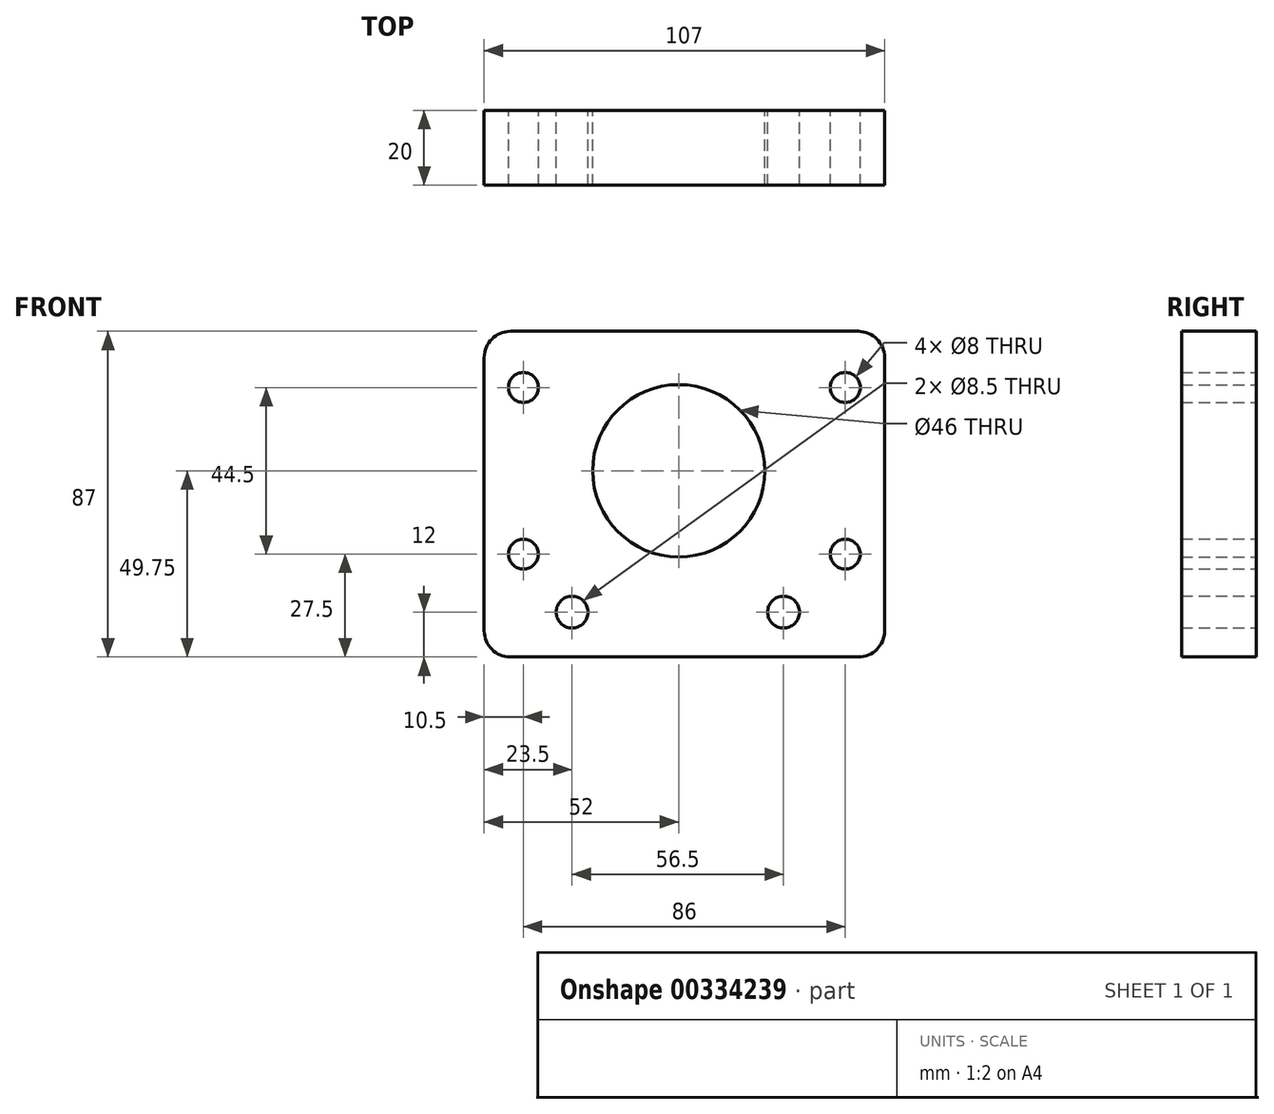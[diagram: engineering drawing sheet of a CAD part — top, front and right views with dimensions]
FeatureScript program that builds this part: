
annotation { "Feature Type Name" : "Feature", "Feature Type Description" : "" }
export const myFeature = defineFeature(function(context is Context, id is Id, definition is map)
    precondition{}
    {
        {
            var Q0;
            Q0=qCreatedBy(makeId("Front.planeOp"),FACE);
            var sketch = newSketch(context, id + "F0", { "sketchPlane" : qUnion([Q0])});
            skCircle(sketch, "E0", {"center": v(0, 0) * mm, "radius": 3.35 * mm});
            skCircle(sketch, "E1", {"center": v(56.5, 0) * mm, "radius": 3.35 * mm});
            skCircle(sketch, "E2", {"center": v(0, -65) * mm, "radius": 4.25 * mm});
            skCircle(sketch, "E3", {"center": v(56.5, -65) * mm, "radius": 4.25 * mm});
            skCircle(sketch, "E4", {"center": v(28.5, -27.25) * mm, "radius": 23 * mm});
            skCircle(sketch, "E5", {"center": v(-13, -49.5) * mm, "radius": 4 * mm});
            skCircle(sketch, "E6", {"center": v(-13, -5) * mm, "radius": 4 * mm});
            skCircle(sketch, "E7", {"center": v(73, -5) * mm, "radius": 4 * mm});
            skCircle(sketch, "E8", {"center": v(73, -49.5) * mm, "radius": 4 * mm});
            skLineSegment(sketch, "E9.bottom", {"start": v(-16.5, 10) * mm, "end": v(76.5, 10) * mm});
            skLineSegment(sketch, "E9.top", {"start": v(-16.5, -77) * mm, "end": v(76.5, -77) * mm});
            skLineSegment(sketch, "E9.left", {"start": v(-23.5, 3) * mm, "end": v(-23.5, -70) * mm});
            skLineSegment(sketch, "E9.right", {"start": v(83.5, 3) * mm, "end": v(83.5, -70) * mm});
            skPoint(sketch, "E10.visualSharp", {"position": v(-23.5, 10) * mm});
            skArc(sketch, "E10.filletArc", {"start": v(-16.5, 10) * mm, "mid": v(-21.45, 7.95) * mm, "end": v(-23.5, 3) * mm});
            skPoint(sketch, "E11.visualSharp", {"position": v(83.5, 10) * mm});
            skArc(sketch, "E11.filletArc", {"start": v(83.5, 3) * mm, "mid": v(81.45, 7.95) * mm, "end": v(76.5, 10) * mm});
            skPoint(sketch, "E12.visualSharp", {"position": v(83.5, -77) * mm});
            skArc(sketch, "E12.filletArc", {"start": v(76.5, -77) * mm, "mid": v(81.45, -74.95) * mm, "end": v(83.5, -70) * mm});
            skPoint(sketch, "E13.visualSharp", {"position": v(-23.5, -77) * mm});
            skArc(sketch, "E13.filletArc", {"start": v(-23.5, -70) * mm, "mid": v(-21.45, -74.95) * mm, "end": v(-16.5, -77) * mm});
            skSolve(sketch);
        }
        {
            var Q0;
            Q0=makeQuery(id+"F0.imprint","IMPRINT",FACE,{"disambiguationData":[TD([[makeQuery(id+"F0.imprint","IMPRINT",EDGE,{"derivedFrom":sQuery(id+"F0.wireOp",EDGE,"E0")}),-1.0]])]});
            var Q1;
            Q1=makeQuery(id+"F0.imprint","IMPRINT",FACE,{"disambiguationData":[TD([[makeQuery(id+"F0.imprint","IMPRINT",EDGE,{"derivedFrom":sQuery(id+"F0.wireOp",EDGE,"E0")}),1.0]])]});
            var Q2;
            Q2=makeQuery(id+"F0.imprint","IMPRINT",FACE,{"disambiguationData":[TD([[makeQuery(id+"F0.imprint","IMPRINT",EDGE,{"derivedFrom":sQuery(id+"F0.wireOp",EDGE,"E1")}),1.0]])]});
            extrude(context, id + "F1", {"entities" : qUnion([Q0, Q1, Q2]), "depth" : 20 * mm});
        }
    });
